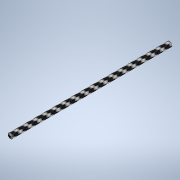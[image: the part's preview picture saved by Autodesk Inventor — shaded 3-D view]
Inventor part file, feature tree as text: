
AUTODESK INVENTOR PART (.ipt)
format: ipt  version: 2020 (Build 240168000, 168)  size: 101,888 bytes
history: native  units: in
note: dims shown in document units (in); Inventor stores cm internally (conversion verified against a paired STEP export)
features: extrude x1, sketch x1
ambient origin geometry x8: Origin, YZ Plane, XZ Plane, XY Plane, X Axis, Y Axis, Z Axis, Center Point
bodies: Solid1 (feature_tree)
feature tree (2):
  extrude  "Extrusion1"  Depth=2.4831in
  sketch  "Sketch1"  dims[d0=0.0787in d1=2.4831in d2=0.0in]
